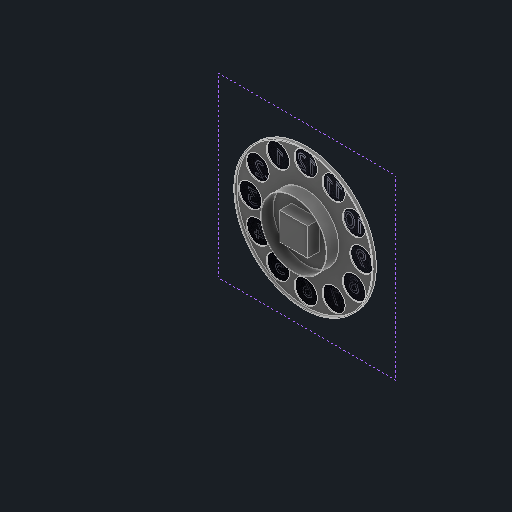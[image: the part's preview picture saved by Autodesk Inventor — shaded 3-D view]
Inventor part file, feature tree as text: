
AUTODESK INVENTOR PART (.ipt)
format: ipt  version: 2023.1 (Build 271208000, 208)  size: 3,794,944 bytes
history: native  units: mm
features: sketch x5, extrude x3, other x1
ambient origin geometry x8: Origin, YZ Plane, XZ Plane, XY Plane, X Axis, Y Axis, Z Axis, Center Point
bodies: Solid1 (feature_tree)
feature tree (9):
  extrude  "Extrusion1"  Depth=50.0mm
  extrude  "Extrusion2"  Depth=120.0mm
  extrude  "Extrusion3"  Depth=2.0mm TaperAngle=0.0deg
  sketch  "Sketch4"  dims[d10=2.0mm]
  sketch  "Sketch5"  dims[d11=5.0mm d12=0.0mm d13=142.0mm d14=1.0mm d15=26.0mm d16=0.0mm d17=60.0mm d18=60.0mm]
  sketch  "Sketch1"  dims[d0=300.0mm d1=50.0mm]
  sketch  "Sketch2"  dims[d2=0.0mm d3=120.0mm]
  sketch  "Sketch3"  dims[d4=120.0mm d6=360.0deg d8=2.0mm d9=0.0mm]
  other  "Image1"
